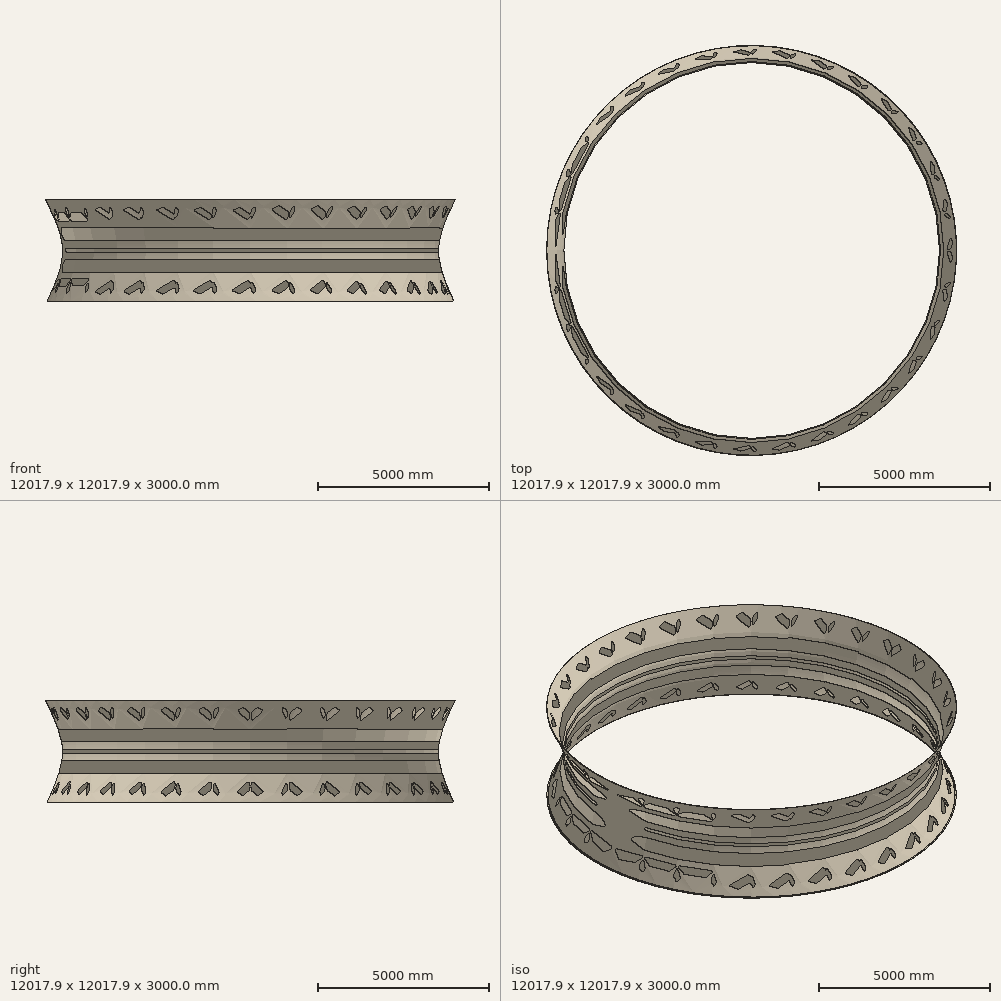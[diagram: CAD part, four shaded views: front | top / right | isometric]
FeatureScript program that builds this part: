
annotation { "Feature Type Name" : "Feature", "Feature Type Description" : "" }
export const myFeature = defineFeature(function(context is Context, id is Id, definition is map)
    precondition{}
    {
        {
            var Q0;
            Q0=qCreatedBy(makeId("Right.planeOp"),FACE);
            var sketch = newSketch(context, id + "F0", { "sketchPlane" : qUnion([Q0])});
            skLineSegment(sketch, "E0", {"start": v(0, 0) * mm, "end": v(6000, 0) * mm, "construction": true});
            skLineSegment(sketch, "E1", {"start": v(6000, 0) * mm, "end": v(6000, 10) * mm});
            skLineSegment(sketch, "E2", {"start": v(6000, 10) * mm, "end": v(5962.15, 10) * mm});
            skLineSegment(sketch, "E3", {"start": v(5950, 10) * mm, "end": v(5950, 0) * mm});
            skLineSegment(sketch, "E4", {"start": v(5950, 0) * mm, "end": v(6000, 0) * mm});
            skLineSegment(sketch, "E5", {"start": v(0, 0) * mm, "end": v(0, 3000) * mm, "construction": true});
            skLineSegment(sketch, "E6", {"start": v(0, 3000) * mm, "end": v(6000, 3000) * mm, "construction": true});
            skLineSegment(sketch, "E7", {"start": v(0, 1500) * mm, "end": v(5500, 1500) * mm, "construction": true});
            skPoint(sketch, "E7.endSnap0", {"position": v(0, 1500) * mm});
            skFitSpline(sketch, "E8", {"points": [v(6000, 3000) * mm, v(5500, 1500) * mm, v(5950, 10) * mm], "startDerivative": vector(-1472.86, -2987.37) * mm, "endDerivative": vector(1376.6, -2992.63) * mm});
            skFitSpline(sketch, "E9.0", {"points": [v(6008.97, 2995.58) * mm, v(5947.6, 2871.1) * mm, v(5855.6, 2684.5) * mm, v(5744.12, 2435.9) * mm, v(5668.86, 2249.58) * mm, v(5604.72, 2063.38) * mm, v(5562.83, 1908.33) * mm, v(5537.61, 1784.37) * mm, v(5523.19, 1691.44) * mm, v(5515.2, 1614.03) * mm, v(5511.39, 1552.12) * mm, v(5509.86, 1505.7) * mm, v(5509.72, 1459.27) * mm, v(5511.33, 1397.36) * mm, v(5516.59, 1319.93) * mm, v(5527.77, 1226.96) * mm, v(5548.7, 1102.93) * mm, v(5585.33, 947.76) * mm, v(5643.25, 761.36) * mm, v(5712.36, 574.78) * mm, v(5815.74, 325.8) * mm, v(5901.73, 138.87) * mm, v(5959.08, 14.18) * mm]});
            skLineSegment(sketch, "E10", {"start": v(5959.08, 14.18) * mm, "end": v(5962.15, 10) * mm});
            skLineSegment(sketch, "E11", {"start": v(6000, 3000) * mm, "end": v(6008.97, 2995.58) * mm});
            skSolve(sketch);
        }
        {
            var Q0;
            Q0=makeQuery(id+"F0.imprint","IMPRINT",FACE,{"disambiguationData":[TD([[makeQuery(id+"F0.imprint","IMPRINT",EDGE,{"derivedFrom":sQuery(id+"F0.wireOp",EDGE,"E1")}),1.0]])]});
            var Q1;
            Q1=sQuery(id+"F0.wireOp",EDGE,"E5");
            revolve(context, id + "F1", {"entities" : qUnion([Q0]), "axis" : qUnion([Q1]), "revolveType" : RevolveType.FULL});
        }
        {
            var Q0;
            Q0=makeQuery(id+"F1.opRevolve","SWEPT_FACE",FACE,{"disambiguationData":[OSD([sQuery(id+"F0.wireOp",EDGE,"E4")])]});
            var sketch = newSketch(context, id + "F2", { "sketchPlane" : qUnion([Q0])});
            skCircle(sketch, "E12", {"center": v(0, 5970) * mm, "radius": 10 * mm});
            skCircle(sketch, "E13", {"center": v(-9.29, -5970) * mm, "radius": 10 * mm});
            skSolve(sketch);
        }
        {
            var Q0;
            Q0=makeQuery(id+"F2.imprint","IMPRINT",FACE,{"disambiguationData":[TD([[makeQuery(id+"F2.imprint","IMPRINT",EDGE,{"derivedFrom":sQuery(id+"F2.wireOp",EDGE,"E13")}),1.0]])]});
            var Q1;
            Q1=makeQuery(id+"F2.imprint","IMPRINT",FACE,{"disambiguationData":[TD([[makeQuery(id+"F2.imprint","IMPRINT",EDGE,{"derivedFrom":sQuery(id+"F2.wireOp",EDGE,"E12")}),1.0]])]});
            extrude(context, id + "F3", {"entities" : qUnion([Q0, Q1]), "operationType" : NewBodyOperationType.REMOVE, "oppositeDirection" : true, "depth" : 25 * mm});
        }
    });
